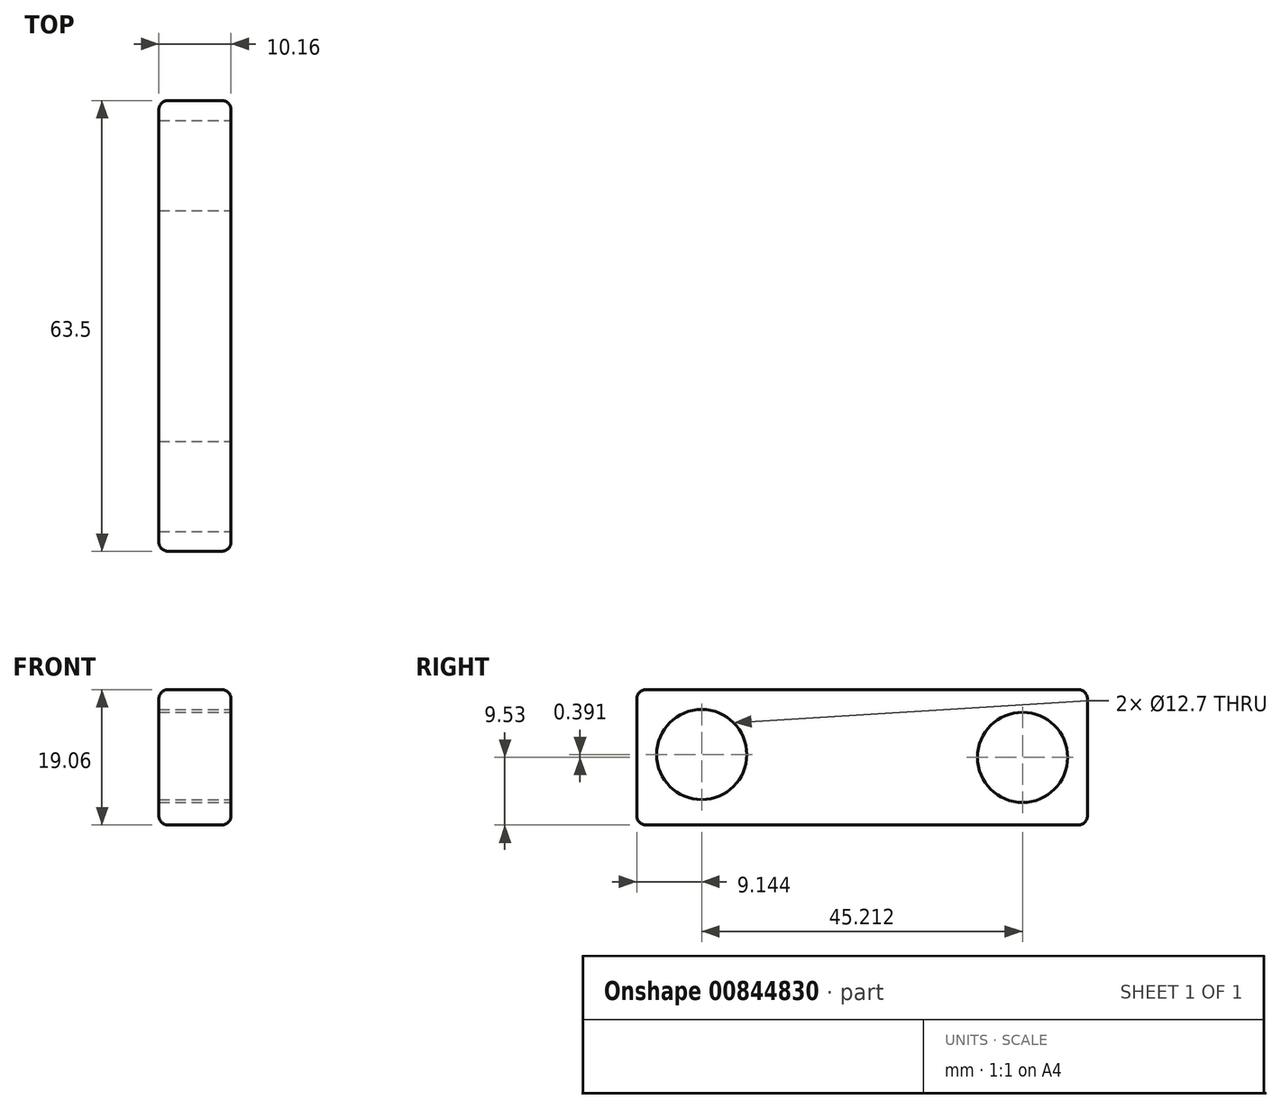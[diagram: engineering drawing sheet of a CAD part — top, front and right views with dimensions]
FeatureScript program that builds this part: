
annotation { "Feature Type Name" : "Feature", "Feature Type Description" : "" }
export const myFeature = defineFeature(function(context is Context, id is Id, definition is map)
    precondition{}
    {
        {
            var Q0;
            Q0=qCreatedBy(makeId("Right.planeOp"),FACE);
            var sketch = newSketch(context, id + "F0", { "sketchPlane" : qUnion([Q0])});
            skLineSegment(sketch, "E0.bottom", {"start": v(31.75, -9.53) * mm, "end": v(-31.75, -9.53) * mm});
            skLineSegment(sketch, "E0.top", {"start": v(31.75, 9.53) * mm, "end": v(-31.75, 9.52) * mm});
            skLineSegment(sketch, "E0.left", {"start": v(31.75, -9.53) * mm, "end": v(31.75, 9.53) * mm});
            skLineSegment(sketch, "E0.right", {"start": v(-31.75, -9.53) * mm, "end": v(-31.75, 9.52) * mm});
            skPoint(sketch, "E0.middle", {"position": v(0, 0) * mm});
            skSolve(sketch);
        }
        {
            var Q0;
            Q0 = qSketchRegion(id + "F0", true);
            extrude(context, id + "F1", {"entities" : qUnion([Q0]), "depth" : 5.08 * mm, "offsetDistance" : 25.4 * mm, "hasSecondDirection" : true, "secondDirectionOppositeDirection" : true, "secondDirectionDepth" : 5.08 * mm});
        }
        {
            var Q0;
            Q0=makeQuery(id+"F1.opExtrude","CAP_FACE",FACE,{"disambiguationData":[OSD([sQuery(id+"F0.wireOp",EDGE,"E0.bottom"),sQuery(id+"F0.wireOp",EDGE,"E0.top"),sQuery(id+"F0.wireOp",EDGE,"E0.left"),sQuery(id+"F0.wireOp",EDGE,"E0.right")])],"isStart":false});
            var sketch = newSketch(context, id + "F2", { "sketchPlane" : qUnion([Q0])});
            skCircle(sketch, "E1", {"center": v(22.6, 0) * mm, "radius": 6.35 * mm});
            skCircle(sketch, "E2", {"center": v(-22.6, 0.4) * mm, "radius": 6.35 * mm});
            skSolve(sketch);
        }
        {
            var Q0;
            Q0 = qSketchRegion(id + "F2", true);
            extrude(context, id + "F3", {"entities" : qUnion([Q0]), "operationType" : NewBodyOperationType.REMOVE, "oppositeDirection" : true, "depth" : 25.4 * mm, "offsetDistance" : 25.4 * mm});
        }
        {
            var Q0;
            Q0=makeQuery(id+"F1.opExtrude","SWEPT_FACE",FACE,{"disambiguationData":[OSD([sQuery(id+"F0.wireOp",EDGE,"E0.top")])]});
            var Q1;
            Q1=makeQuery(id+"F1.opExtrude","SWEPT_FACE",FACE,{"disambiguationData":[OSD([sQuery(id+"F0.wireOp",EDGE,"E0.left")])]});
            var Q2;
            Q2=makeQuery(id+"F1.opExtrude","SWEPT_FACE",FACE,{"disambiguationData":[OSD([sQuery(id+"F0.wireOp",EDGE,"E0.bottom")])]});
            var Q3;
            Q3=makeQuery(id+"F1.opExtrude","SWEPT_FACE",FACE,{"disambiguationData":[OSD([sQuery(id+"F0.wireOp",EDGE,"E0.right")])]});
            fillet(context, id + "F4", {"entities" : qUnion([Q0, Q1, Q2, Q3]), "radius" : 1.27 * mm, "tangentPropagation" : true, "allowEdgeOverflow" : false});
        }
    });
